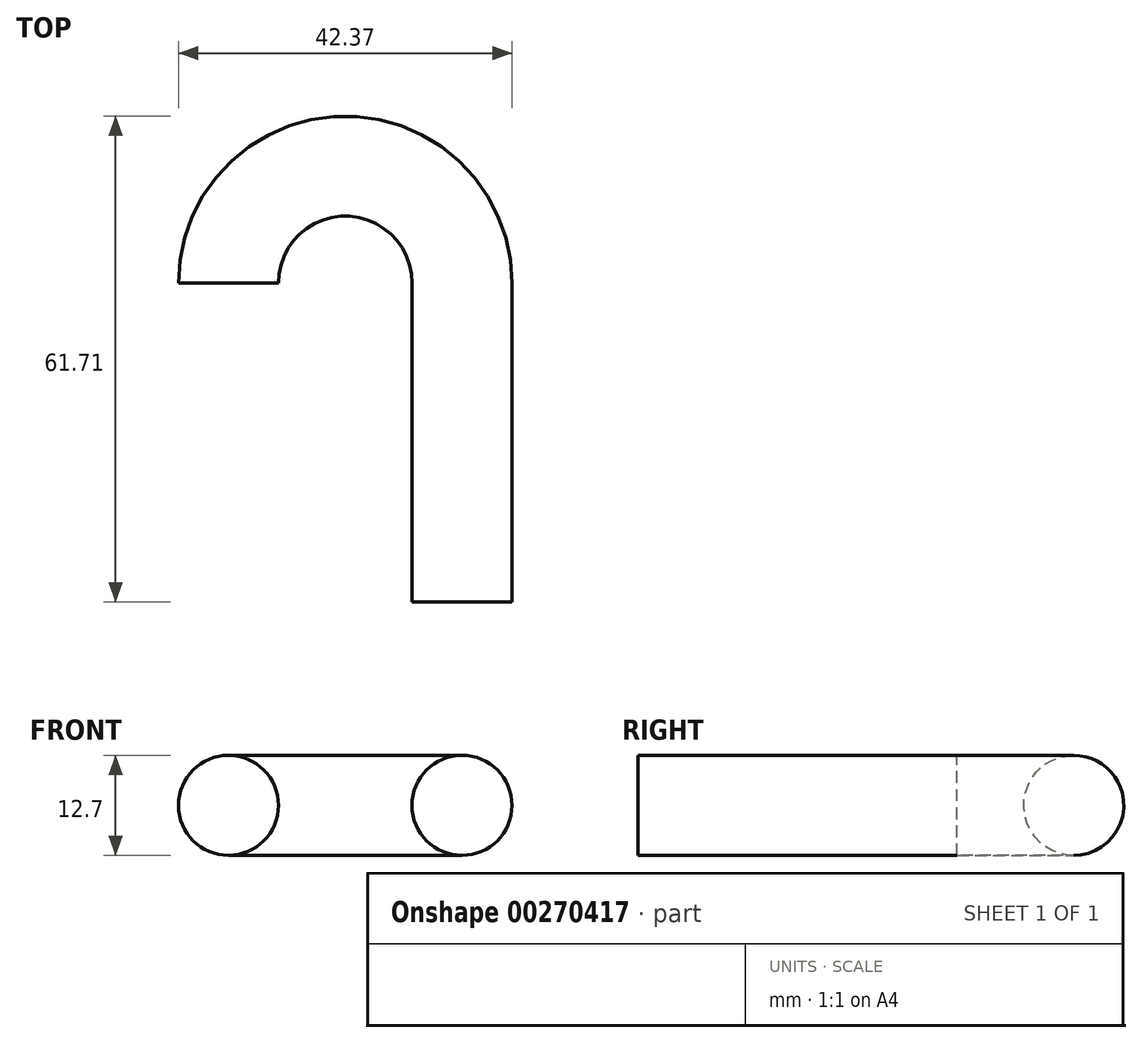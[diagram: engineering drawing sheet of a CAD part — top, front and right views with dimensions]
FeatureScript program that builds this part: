
annotation { "Feature Type Name" : "Feature", "Feature Type Description" : "" }
export const myFeature = defineFeature(function(context is Context, id is Id, definition is map)
    precondition{}
    {
        {
            var Q0;
            Q0=qCreatedBy(makeId("Top.planeOp"),FACE);
            var sketch = newSketch(context, id + "F0", { "sketchPlane" : qUnion([Q0])});
            skLineSegment(sketch, "E0", {"start": v(0, 0) * mm, "end": v(0, 40.52) * mm});
            skArc(sketch, "E1", {"start": v(0, 40.52) * mm, "mid": v(-14.83, 55.36) * mm, "end": v(-29.67, 40.52) * mm});
            skSolve(sketch);
        }
        {
            var Q0;
            Q0=qCreatedBy(makeId("Front.planeOp"),FACE);
            var sketch = newSketch(context, id + "F1", { "sketchPlane" : qUnion([Q0])});
            skCircle(sketch, "E2", {"center": v(0, 0) * mm, "radius": 6.35 * mm});
            skSolve(sketch);
        }
        {
            var Q0;
            Q0=makeQuery(id+"F1.imprint","IMPRINT",FACE,{"disambiguationData":[TD([[makeQuery(id+"F1.imprint","IMPRINT",EDGE,{"derivedFrom":sQuery(id+"F1.wireOp",EDGE,"E2")}),1.0]])]});
            var Q1;
            Q1=sQuery(id+"F0.wireOp",EDGE,"E0");
            var Q2;
            Q2=sQuery(id+"F0.wireOp",EDGE,"E1");
            sweep(context, id + "F2", {"profiles" : qUnion([Q0]), "path" : qUnion([Q1, Q2])});
        }
    });
